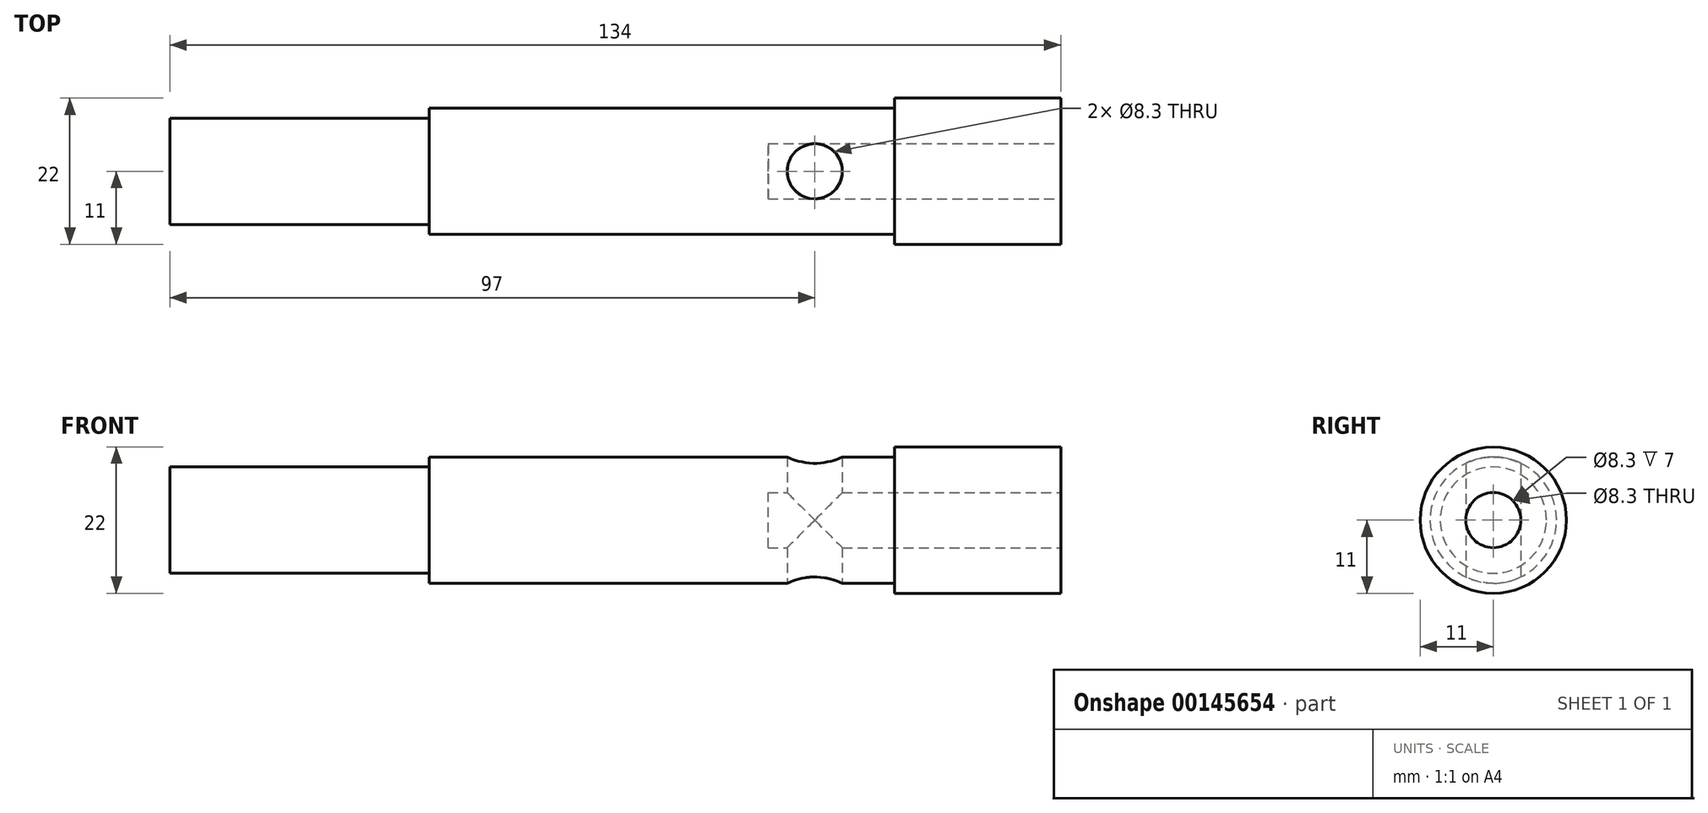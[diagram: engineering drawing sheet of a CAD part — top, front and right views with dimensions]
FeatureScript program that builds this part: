
annotation { "Feature Type Name" : "Feature", "Feature Type Description" : "" }
export const myFeature = defineFeature(function(context is Context, id is Id, definition is map)
    precondition{}
    {
        {
            var Q0;
            Q0=qCreatedBy(makeId("Front.planeOp"),FACE);
            var sketch = newSketch(context, id + "F0", { "sketchPlane" : qUnion([Q0])});
            skLineSegment(sketch, "E0", {"start": v(-58.13, 0) * mm, "end": v(0, 0) * mm, "construction": true});
            skLineSegment(sketch, "E1.bottom", {"start": v(0, 0) * mm, "end": v(-25, 0) * mm});
            skLineSegment(sketch, "E1.top", {"start": v(0, 11) * mm, "end": v(-25, 11) * mm});
            skLineSegment(sketch, "E1.left", {"start": v(0, 0) * mm, "end": v(0, 11) * mm});
            skLineSegment(sketch, "E1.right", {"start": v(-25, 0) * mm, "end": v(-25, 11) * mm});
            skLineSegment(sketch, "E2.bottom", {"start": v(-25, 0) * mm, "end": v(-37, 0) * mm});
            skLineSegment(sketch, "E2.top", {"start": v(-25, 9.5) * mm, "end": v(-37, 9.5) * mm});
            skLineSegment(sketch, "E2.left", {"start": v(-25, 0) * mm, "end": v(-25, 9.5) * mm});
            skLineSegment(sketch, "E2.right", {"start": v(-37, 0) * mm, "end": v(-37, 9.5) * mm});
            skLineSegment(sketch, "E3.bottom", {"start": v(-37, 0) * mm, "end": v(-95, 0) * mm});
            skLineSegment(sketch, "E3.top", {"start": v(-37, 9.5) * mm, "end": v(-95, 9.5) * mm});
            skLineSegment(sketch, "E3.right", {"start": v(-95, 0) * mm, "end": v(-95, 9.5) * mm});
            skLineSegment(sketch, "E4.bottom", {"start": v(-95, 0) * mm, "end": v(-134, 0) * mm});
            skLineSegment(sketch, "E4.top", {"start": v(-95, 8) * mm, "end": v(-134, 8) * mm});
            skLineSegment(sketch, "E4.left", {"start": v(-95, 0) * mm, "end": v(-95, 8) * mm});
            skLineSegment(sketch, "E4.right", {"start": v(-134, 0) * mm, "end": v(-134, 8) * mm});
            skLineSegment(sketch, "E5.MirrorCS", {"start": v(-25, 0) * mm, "end": v(-25, -11) * mm});
            skLineSegment(sketch, "E6.MirrorCS", {"start": v(-37, 0) * mm, "end": v(-37, -9.5) * mm});
            skLineSegment(sketch, "E7.MirrorCS", {"start": v(-95, 0) * mm, "end": v(-95, -8) * mm});
            skLineSegment(sketch, "E8.MirrorCS", {"start": v(-134, 0) * mm, "end": v(-134, -8) * mm});
            skLineSegment(sketch, "E9.MirrorCS", {"start": v(-95, 0) * mm, "end": v(-95, -9.5) * mm});
            skLineSegment(sketch, "E10.MirrorCS", {"start": v(-37, -9.5) * mm, "end": v(-95, -9.5) * mm});
            skLineSegment(sketch, "E11.MirrorCS", {"start": v(-25, 0) * mm, "end": v(-25, -9.5) * mm});
            skLineSegment(sketch, "E12.MirrorCS", {"start": v(-25, -9.5) * mm, "end": v(-37, -9.5) * mm});
            skLineSegment(sketch, "E13.MirrorCS", {"start": v(0, 0) * mm, "end": v(0, -11) * mm});
            skLineSegment(sketch, "E14.MirrorCS", {"start": v(0, -11) * mm, "end": v(-25, -11) * mm});
            skLineSegment(sketch, "E15.MirrorCS", {"start": v(-95, -8) * mm, "end": v(-134, -8) * mm});
            skSolve(sketch);
        }
        {
            var Q0;
            Q0=makeQuery(id+"F0.imprint","IMPRINT",FACE,{"disambiguationData":[TD([[makeQuery(id+"F0.imprint","IMPRINT",EDGE,{"derivedFrom":sQuery(id+"F0.wireOp",EDGE,"E1.bottom")}),-1.0]])]});
            var Q1;
            Q1=makeQuery(id+"F0.imprint","IMPRINT",FACE,{"disambiguationData":[TD([[makeQuery(id+"F0.imprint","IMPRINT",EDGE,{"derivedFrom":sQuery(id+"F0.wireOp",EDGE,"E2.top")}),1.0]])]});
            var Q2;
            Q2=makeQuery(id+"F0.imprint","IMPRINT",FACE,{"disambiguationData":[TD([[makeQuery(id+"F0.imprint","IMPRINT",EDGE,{"derivedFrom":sQuery(id+"F0.wireOp",EDGE,"E3.top")}),1.0]])]});
            var Q3;
            Q3=makeQuery(id+"F0.imprint","IMPRINT",FACE,{"disambiguationData":[TD([[makeQuery(id+"F0.imprint","IMPRINT",EDGE,{"derivedFrom":sQuery(id+"F0.wireOp",EDGE,"E4.top")}),1.0]])]});
            var Q4;
            Q4=sQuery(id+"F0.wireOp",EDGE,"E1.bottom");
            revolve(context, id + "F1", {"entities" : qUnion([Q0, Q1, Q2, Q3]), "axis" : qUnion([Q4]), "revolveType" : RevolveType.FULL});
        }
        {
            var Q0;
            Q0=qCreatedBy(makeId("Top.planeOp"),FACE);
            var sketch = newSketch(context, id + "F2", { "sketchPlane" : qUnion([Q0])});
            skLineSegment(sketch, "E16.0", {"start": v(-37, 0) * mm, "end": v(-95, 0) * mm});
            skLineSegment(sketch, "E17.0", {"start": v(-25, 0) * mm, "end": v(-37, 0) * mm});
            skCircle(sketch, "E18", {"center": v(-37, 0) * mm, "radius": 4.15 * mm});
            skSolve(sketch);
        }
        {
            var Q0;
            {var subQ0=sQuery(id+"F2.wireOp",EDGE,"E17.0");var subQ1=sQuery(id+"F2.wireOp",EDGE,"E16.0");var subQ2=makeQuery(id+"F2.imprint","INTERSECT",VERTEX,{"derivedFrom":[subQ1,subQ0]});Q0=makeQuery(id+"F2.imprint","IMPRINT",FACE,{"disambiguationData":[TD([[makeQuery(id+"F2.imprint","IMPRINT",EDGE,{"disambiguationData":[TD([[subQ2,-1.0]])],"derivedFrom":subQ1}),-1.0]])]});}
            var Q1;
            {var subQ0=sQuery(id+"F2.wireOp",EDGE,"E17.0");var subQ1=sQuery(id+"F2.wireOp",EDGE,"E16.0");var subQ2=makeQuery(id+"F2.imprint","INTERSECT",VERTEX,{"derivedFrom":[subQ1,subQ0]});Q1=makeQuery(id+"F2.imprint","IMPRINT",FACE,{"disambiguationData":[TD([[makeQuery(id+"F2.imprint","IMPRINT",EDGE,{"disambiguationData":[TD([[subQ2,-1.0]])],"derivedFrom":subQ1}),1.0]])]});}
            extrude(context, id + "F3", {"entities" : qUnion([Q0, Q1]), "operationType" : NewBodyOperationType.REMOVE, "endBound" : BoundingType.THROUGH_ALL, "depth" : 25 * mm, "hasSecondDirection" : true, "secondDirectionBound" : SecondDirectionBoundingType.THROUGH_ALL, "secondDirectionOppositeDirection" : true, "secondDirectionDepth" : 25 * mm});
        }
        {
            var Q0;
            Q0=qCreatedBy(makeId("Right.planeOp"),FACE);
            var sketch = newSketch(context, id + "F4", { "sketchPlane" : qUnion([Q0])});
            skCircle(sketch, "E19", {"center": v(0, 0) * mm, "radius": 4.15 * mm});
            skSolve(sketch);
        }
        {
            var Q0;
            Q0=qSketchRegion(id+"F4",true);
            extrude(context, id + "F5", {"entities" : qUnion([Q0]), "operationType" : NewBodyOperationType.REMOVE, "oppositeDirection" : true, "depth" : 44 * mm});
        }
    });
